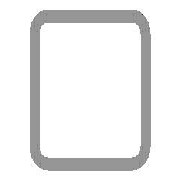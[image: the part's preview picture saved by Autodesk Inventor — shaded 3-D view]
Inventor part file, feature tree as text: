
AUTODESK INVENTOR PART (.ipt)
format: ipt  version: 2018 (Build 220112000, 112)  size: 129,536 bytes
history: native  units: mm (DEFAULTED — no unit token found)
features: other x4, sketch x3, extrude x1, plane x1
ambient origin geometry x8: Origin, YZ Plane, XZ Plane, XY Plane, X Axis, Y Axis, Z Axis, Center Point
bodies: Solid1 (feature_tree)
feature tree (9):
  other  "Tubolare horizontal - Taglio"
  other  "Driven Length"
  other  "Piano iniziale"
  other  "Piano finale"
  extrude  "Corpo"  TaperAngle=0.0deg  [1 undecoded]
  sketch  "Schizzo"
  sketch  "Sketch3"  dims[d3=370.0mm d4=0.0mm]
  plane  "Work Plane3"
  sketch  "Sketch4"  dims[d7=4.0mm d9=40.0mm d11=40.0mm d12=2.0mm d13=-0.0mm d14=370.0mm d15=20.0mm d16=20.0mm d17=90.0deg d18=370.0mm]
note: 1 required parameter value undecoded (feature->parameter linkage not recoverable at this tier; creation-order binding heuristic only, values carry confidence <= 0.55)
